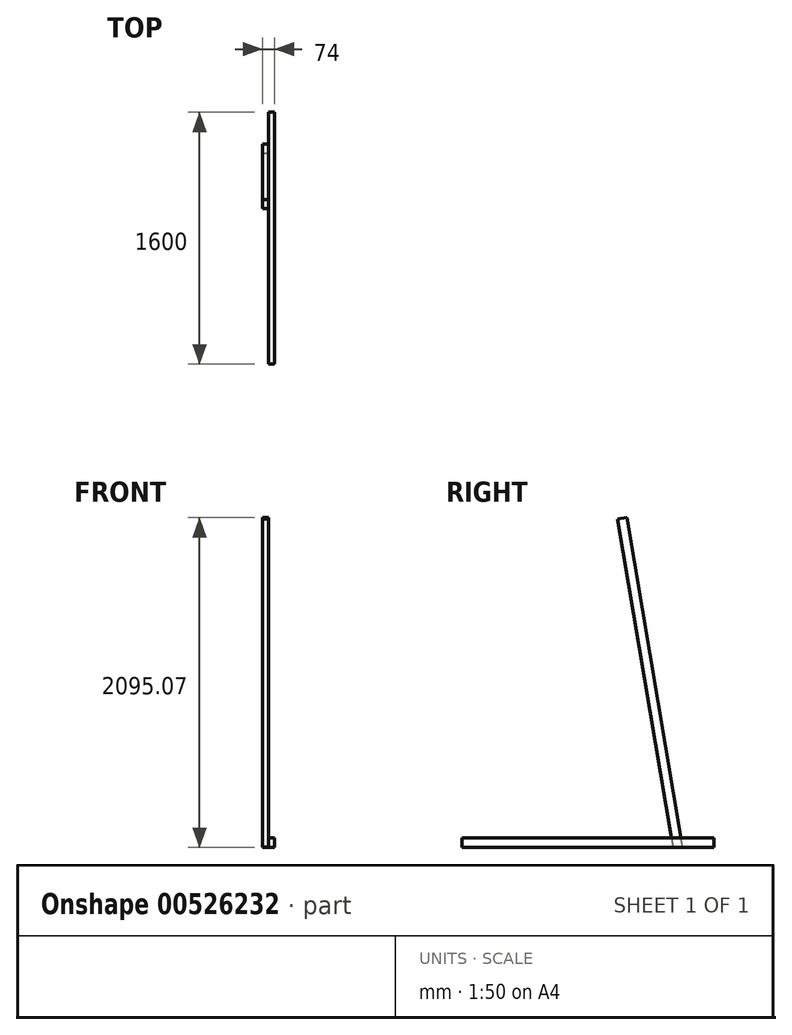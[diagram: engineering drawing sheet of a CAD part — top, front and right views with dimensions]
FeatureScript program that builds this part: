
annotation { "Feature Type Name" : "Feature", "Feature Type Description" : "" }
export const myFeature = defineFeature(function(context is Context, id is Id, definition is map)
    precondition{}
    {
        {
            var Q0;
            Q0=qCreatedBy(makeId("Right.planeOp"),FACE);
            var sketch = newSketch(context, id + "F0", { "sketchPlane" : qUnion([Q0])});
            skLineSegment(sketch, "E0.bottom", {"start": v(30, -88.5) * mm, "end": v(-30, -88.5) * mm});
            skLineSegment(sketch, "E0.top", {"start": v(30, 88.5) * mm, "end": v(-30, 88.5) * mm});
            skLineSegment(sketch, "E0.left", {"start": v(30, -88.5) * mm, "end": v(30, 88.5) * mm});
            skLineSegment(sketch, "E0.right", {"start": v(-30, -88.5) * mm, "end": v(-30, 88.5) * mm});
            skPoint(sketch, "E0.middle", {"position": v(0, 0) * mm});
            skLineSegment(sketch, "E1", {"start": v(0, 0) * mm, "end": v(0, -249.99) * mm, "construction": true});
            skLineSegment(sketch, "E2", {"start": v(600, -2050) * mm, "end": v(295.79, -249.99) * mm});
            skLineSegment(sketch, "E3", {"start": v(0, -2050) * mm, "end": v(600, -2050) * mm, "construction": true});
            skLineSegment(sketch, "E4.MirrorCS", {"start": v(0, -2050) * mm, "end": v(-600, -2050) * mm, "construction": true});
            skLineSegment(sketch, "E5", {"start": v(0, -249.99) * mm, "end": v(295.79, -249.99) * mm});
            skLineSegment(sketch, "E6", {"start": v(0, 0) * mm, "end": v(0, 249.92) * mm, "construction": true});
            skLineSegment(sketch, "E7", {"start": v(0, 0) * mm, "end": v(5.74, 249.92) * mm});
            skLineSegment(sketch, "E8", {"start": v(5.74, 249.92) * mm, "end": v(3.64, 158.46) * mm});
            skLineSegment(sketch, "E9", {"start": v(3.64, 158.46) * mm, "end": v(5.74, 249.92) * mm});
            skLineSegment(sketch, "E10.MirrorCS", {"start": v(-5.74, 249.92) * mm, "end": v(-3.64, 158.46) * mm});
            skLineSegment(sketch, "E11", {"start": v(-3.64, 158.46) * mm, "end": v(-5.74, 249.92) * mm});
            skLineSegment(sketch, "E12", {"start": v(5.74, 249.92) * mm, "end": v(5.74, 249.92) * mm});
            skLineSegment(sketch, "E13", {"start": v(-5.74, 249.92) * mm, "end": v(-5.74, 249.92) * mm});
            skArc(sketch, "E14", {"start": v(-3.64, 158.46) * mm, "mid": v(0, -158.5) * mm, "end": v(3.64, 158.46) * mm});
            skArc(sketch, "E15", {"start": v(-5.74, 249.92) * mm, "mid": v(-167, 186.02) * mm, "end": v(-247.86, 32.54) * mm});
            skLineSegment(sketch, "E16.MirrorCS", {"start": v(0, -249.99) * mm, "end": v(-295.79, -249.99) * mm});
            skLineSegment(sketch, "E17.MirrorCS", {"start": v(-600, -2050) * mm, "end": v(-295.79, -249.99) * mm});
            skArc(sketch, "E18", {"start": v(245.9, 45.07) * mm, "mid": v(162.24, 190.2) * mm, "end": v(5.74, 249.92) * mm});
            skLineSegment(sketch, "E19", {"start": v(0, -249.99) * mm, "end": v(0, -2050) * mm, "construction": true});
            skLineSegment(sketch, "E20.bottom", {"start": v(0, -2050) * mm, "end": v(800, -2050) * mm});
            skLineSegment(sketch, "E20.top", {"start": v(0, -1990) * mm, "end": v(800, -1990) * mm});
            skLineSegment(sketch, "E20.left", {"start": v(0, -2050) * mm, "end": v(0, -1990) * mm});
            skLineSegment(sketch, "E20.right", {"start": v(800, -2050) * mm, "end": v(800, -1990) * mm});
            skLineSegment(sketch, "E21.MirrorCS", {"start": v(0, -1990) * mm, "end": v(-800, -1990) * mm});
            skLineSegment(sketch, "E22.MirrorCS", {"start": v(0, -2050) * mm, "end": v(-800, -2050) * mm});
            skLineSegment(sketch, "E23.MirrorCS", {"start": v(-800, -2050) * mm, "end": v(-800, -1990) * mm});
            skLineSegment(sketch, "E24", {"start": v(245.92, 45.07) * mm, "end": v(188.08, 35.3) * mm});
            skLineSegment(sketch, "E25", {"start": v(188.08, 35.3) * mm, "end": v(540.5, -2050) * mm});
            skLineSegment(sketch, "E26", {"start": v(540.5, -2050) * mm, "end": v(598.35, -2040.22) * mm});
            skLineSegment(sketch, "E27", {"start": v(-295.79, -249.99) * mm, "end": v(-245.92, 45.07) * mm});
            skLineSegment(sketch, "E28", {"start": v(295.79, -249.99) * mm, "end": v(245.92, 45.07) * mm});
            skSolve(sketch);
        }
        {
            var Q0;
            {var subQ5=sQuery(id+"F0.wireOp",EDGE,"E23.MirrorCS");Q0=makeQuery(id+"F0.imprint","IMPRINT",FACE,{"disambiguationData":[TD([[makeQuery(id+"F0.imprint","IMPRINT",EDGE,{"derivedFrom":subQ5}),-1.0]])]});}
            var Q1;
            {var subQ5=sQuery(id+"F0.wireOp",EDGE,"E20.left");Q1=makeQuery(id+"F0.imprint","IMPRINT",FACE,{"disambiguationData":[TD([[makeQuery(id+"F0.imprint","IMPRINT",EDGE,{"derivedFrom":subQ5}),1.0]])]});}
            var Q2;
            {var subQ0=sQuery(id+"F0.wireOp",EDGE,"E20.left");Q2=makeQuery(id+"F0.imprint","IMPRINT",FACE,{"disambiguationData":[TD([[makeQuery(id+"F0.imprint","IMPRINT",EDGE,{"derivedFrom":subQ0}),-1.0]])]});}
            var Q3;
            {var subQ0=sQuery(id+"F0.wireOp",EDGE,"E26");Q3=makeQuery(id+"F0.imprint","IMPRINT",FACE,{"disambiguationData":[TD([[makeQuery(id+"F0.imprint","IMPRINT",EDGE,{"derivedFrom":subQ0}),1.0]])]});}
            var Q4;
            {var subQ0=sQuery(id+"F0.wireOp",EDGE,"E20.right");Q4=makeQuery(id+"F0.imprint","IMPRINT",FACE,{"disambiguationData":[TD([[makeQuery(id+"F0.imprint","IMPRINT",EDGE,{"derivedFrom":subQ0}),1.0]])]});}
            var Q5;
            {var subQ3=sQuery(id+"F0.wireOp",EDGE,"E26");Q5=makeQuery(id+"F0.imprint","IMPRINT",FACE,{"disambiguationData":[TD([[makeQuery(id+"F0.imprint","IMPRINT",EDGE,{"derivedFrom":subQ3}),-1.0]])]});}
            extrude(context, id + "F1", {"entities" : qUnion([Q0, Q1, Q2, Q3, Q4, Q5]), "depth" : 37 * mm, "offsetDistance" : 25 * mm});
        }
        {
            var Q0;
            {var subQ0=sQuery(id+"F0.wireOp",EDGE,"E24");Q0=makeQuery(id+"F0.imprint","IMPRINT",FACE,{"disambiguationData":[TD([[makeQuery(id+"F0.imprint","IMPRINT",EDGE,{"derivedFrom":subQ0}),1.0]])]});}
            var Q1;
            {var subQ0=sQuery(id+"F0.wireOp",EDGE,"E5");var subQ1=sQuery(id+"F0.wireOp",EDGE,"E2");var subQ2=makeQuery(id+"F0.imprint","INTERSECT",VERTEX,{"derivedFrom":[subQ1,subQ0]});Q1=makeQuery(id+"F0.imprint","IMPRINT",FACE,{"disambiguationData":[TD([[makeQuery(id+"F0.imprint","IMPRINT",EDGE,{"disambiguationData":[TD([[subQ2,1.0]])],"derivedFrom":subQ1}),1.0]])]});}
            var Q2;
            {var subQ0=sQuery(id+"F0.wireOp",EDGE,"E26");Q2=makeQuery(id+"F0.imprint","IMPRINT",FACE,{"disambiguationData":[TD([[makeQuery(id+"F0.imprint","IMPRINT",EDGE,{"derivedFrom":subQ0}),1.0]])]});}
            extrude(context, id + "F2", {"entities" : qUnion([Q0, Q1, Q2]), "operationType" : NewBodyOperationType.ADD, "oppositeDirection" : true, "depth" : 37 * mm, "offsetDistance" : 25 * mm});
        }
    });
